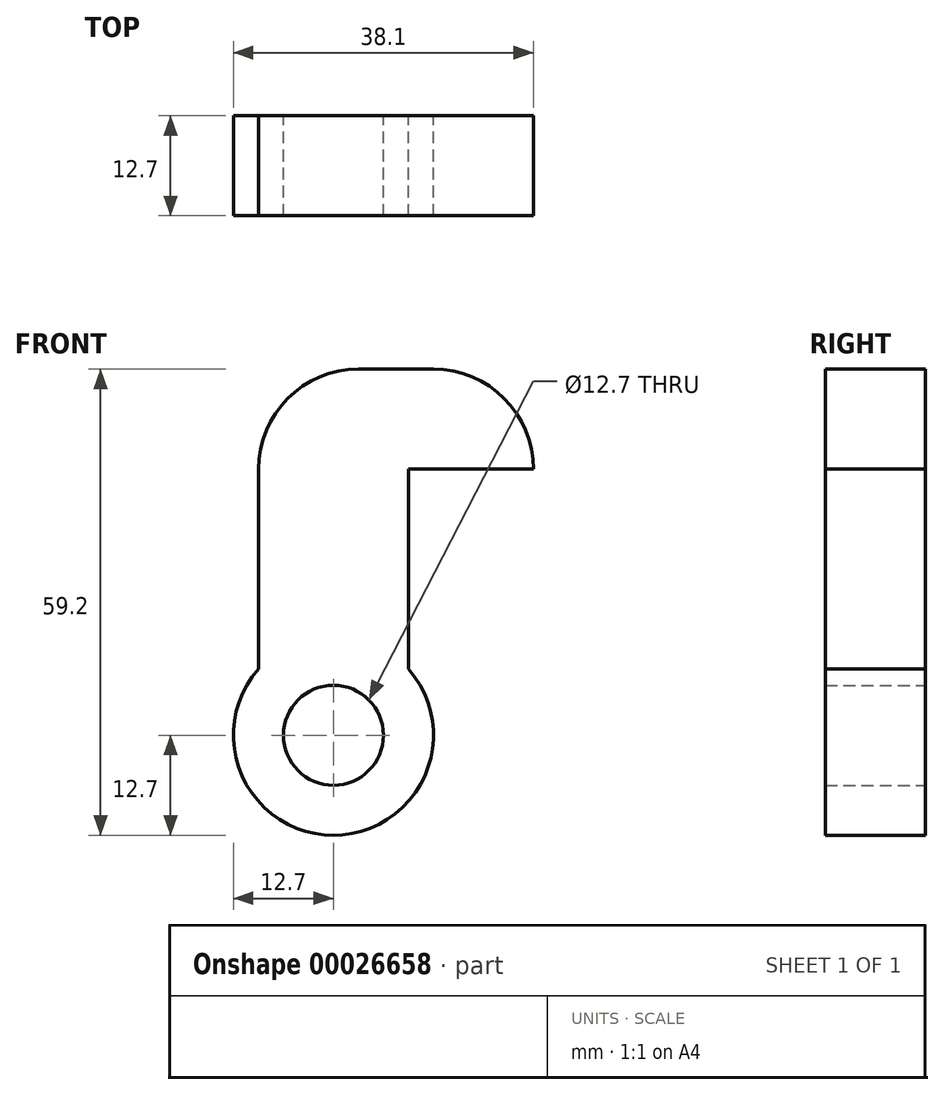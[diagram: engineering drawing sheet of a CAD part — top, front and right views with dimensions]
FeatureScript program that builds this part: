
annotation { "Feature Type Name" : "Feature", "Feature Type Description" : "" }
export const myFeature = defineFeature(function(context is Context, id is Id, definition is map)
    precondition{}
    {
        {
            var Q0;
            Q0=qCreatedBy(makeId("Front.planeOp"),FACE);
            var sketch = newSketch(context, id + "F0", { "sketchPlane" : qUnion([Q0])});
            skCircle(sketch, "E0", {"center": v(-11.6, 7.69) * mm, "radius": 6.35 * mm});
            skCircle(sketch, "E1", {"center": v(-11.6, 7.69) * mm, "radius": 12.7 * mm});
            skLineSegment(sketch, "E2", {"start": v(-21.12, 16.1) * mm, "end": v(-21.12, 41.49) * mm});
            skLineSegment(sketch, "E3", {"start": v(-2.07, 16.09) * mm, "end": v(-2.07, 41.49) * mm});
            skLineSegment(sketch, "E4", {"start": v(-8.42, 54.19) * mm, "end": v(-2.07, 54.19) * mm});
            skLineSegment(sketch, "E5", {"start": v(13.8, 41.49) * mm, "end": v(13.8, 41.49) * mm});
            skLineSegment(sketch, "E6", {"start": v(13.8, 41.49) * mm, "end": v(-2.07, 41.49) * mm});
            skLineSegment(sketch, "E7", {"start": v(-2.07, 54.19) * mm, "end": v(1.1, 54.19) * mm});
            skPoint(sketch, "E8.visualSharp", {"position": v(-21.12, 54.19) * mm});
            skArc(sketch, "E8.filletArc", {"start": v(-8.42, 54.19) * mm, "mid": v(-17.4, 50.47) * mm, "end": v(-21.12, 41.49) * mm});
            skPoint(sketch, "E9.visualSharp", {"position": v(13.8, 54.19) * mm});
            skArc(sketch, "E9.filletArc", {"start": v(13.8, 41.49) * mm, "mid": v(10.08, 50.47) * mm, "end": v(1.1, 54.19) * mm});
            skSolve(sketch);
        }
        {
            var Q0;
            Q0=makeQuery(id+"F0.imprint","IMPRINT",FACE,{"disambiguationData":[TD([[makeQuery(id+"F0.imprint","IMPRINT",EDGE,{"derivedFrom":sQuery(id+"F0.wireOp",EDGE,"E0")}),-1.0]])]});
            var Q1;
            {var subQ1=sQuery(id+"F0.wireOp",EDGE,"E2");Q1=makeQuery(id+"F0.imprint","IMPRINT",FACE,{"disambiguationData":[TD([[makeQuery(id+"F0.imprint","IMPRINT",EDGE,{"derivedFrom":subQ1}),-1.0]])]});}
            extrude(context, id + "F1", {"entities" : qUnion([Q0, Q1]), "depth" : 12.7 * mm});
        }
    });
